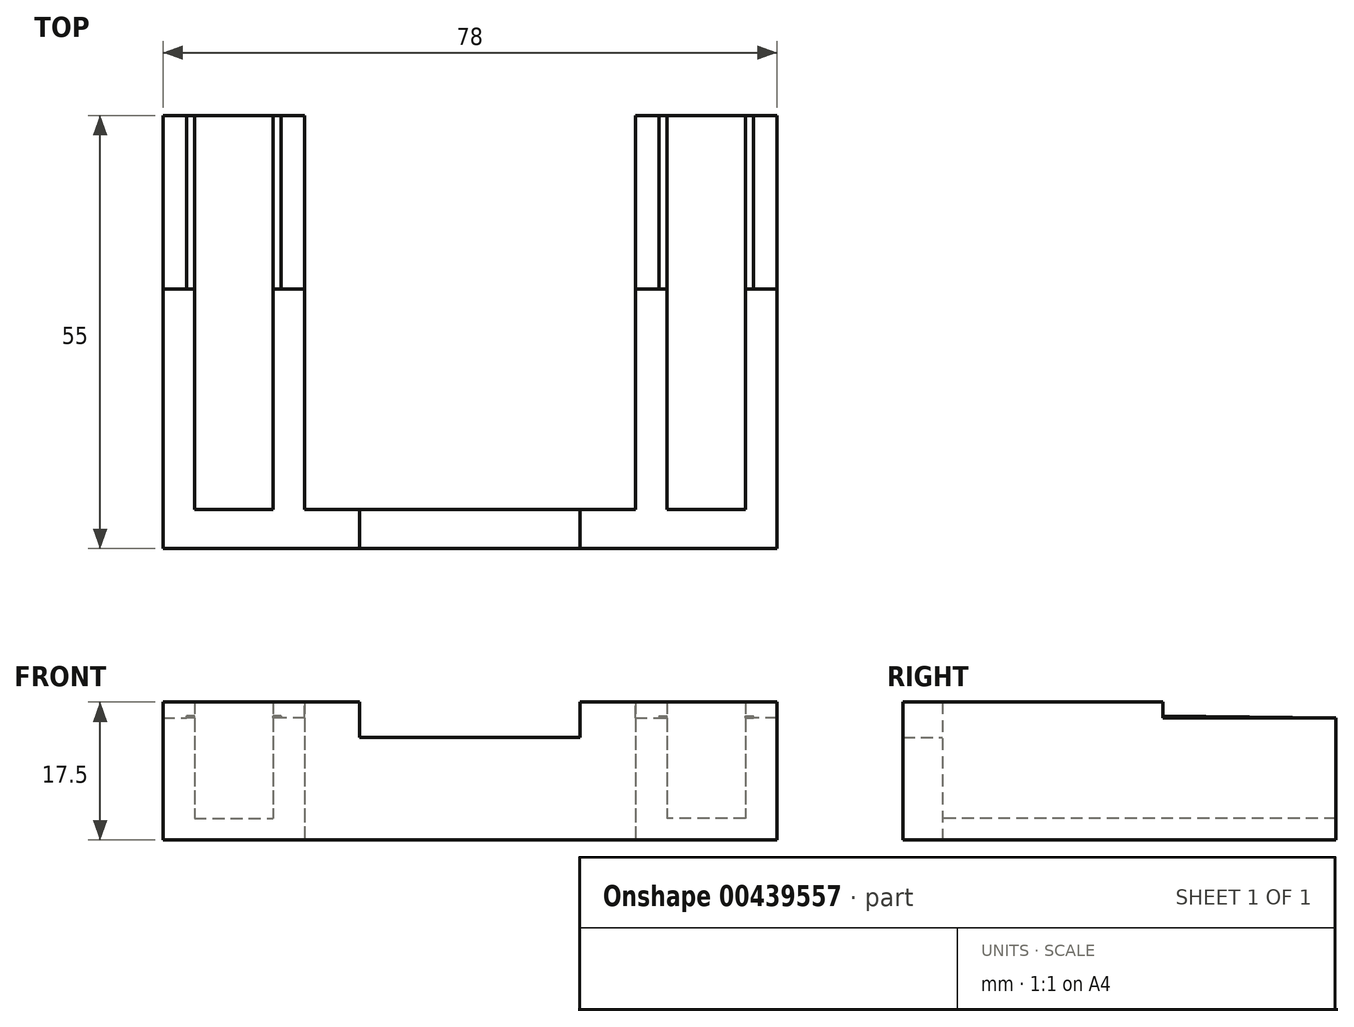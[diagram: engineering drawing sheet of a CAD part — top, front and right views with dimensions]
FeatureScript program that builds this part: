
annotation { "Feature Type Name" : "Feature", "Feature Type Description" : "" }
export const myFeature = defineFeature(function(context is Context, id is Id, definition is map)
    precondition{}
    {
        {
            var Q0;
            Q0=qCreatedBy(makeId("Front.planeOp"),FACE);
            var sketch = newSketch(context, id + "F0", { "sketchPlane" : qUnion([Q0])});
            skLineSegment(sketch, "E0.bottom", {"start": v(-35, 2) * mm, "end": v(-25, 2) * mm});
            skLineSegment(sketch, "E0.top", {"start": v(-35, -2) * mm, "end": v(-25, -2) * mm});
            skLineSegment(sketch, "E1.bottom", {"start": v(-39, 7.75) * mm, "end": v(-35, 7.75) * mm});
            skLineSegment(sketch, "E1.top", {"start": v(-39, -7.75) * mm, "end": v(-35, -7.75) * mm});
            skLineSegment(sketch, "E1.left", {"start": v(-39, 7.75) * mm, "end": v(-39, -7.75) * mm});
            skLineSegment(sketch, "E1.right", {"start": v(-35, 7.75) * mm, "end": v(-35, 2) * mm});
            skLineSegment(sketch, "E2.bottom", {"start": v(-21, 7.75) * mm, "end": v(-25, 7.75) * mm});
            skLineSegment(sketch, "E2.top", {"start": v(-21, -7.75) * mm, "end": v(-25, -7.75) * mm});
            skLineSegment(sketch, "E2.left", {"start": v(-21, 7.75) * mm, "end": v(-21, -7.75) * mm});
            skLineSegment(sketch, "E2.right", {"start": v(-25, 7.75) * mm, "end": v(-25, 2) * mm});
            skLineSegment(sketch, "E3.trimOffspring", {"start": v(-25, -2) * mm, "end": v(-25, -7.75) * mm});
            skLineSegment(sketch, "E4.trimOffspring", {"start": v(-35, -2) * mm, "end": v(-35, -7.75) * mm});
            skPoint(sketch, "E5.trimOffspring.start.orphan", {"position": v(-21, -2) * mm});
            skPoint(sketch, "E6.orphan", {"position": v(-39, 2) * mm});
            skPoint(sketch, "E7.orphan", {"position": v(-21, 2) * mm});
            skPoint(sketch, "E8.visualSharp", {"position": v(-39, 7.75) * mm});
            skPoint(sketch, "E9.visualSharp", {"position": v(-35, 7.75) * mm});
            skPoint(sketch, "E10.visualSharp", {"position": v(-35, 2) * mm});
            skPoint(sketch, "E11.visualSharp", {"position": v(-25, 2) * mm});
            skPoint(sketch, "E12.visualSharp", {"position": v(-25, 7.75) * mm});
            skPoint(sketch, "E13.visualSharp", {"position": v(-21, 7.75) * mm});
            skPoint(sketch, "E14.visualSharp", {"position": v(-21, -7.75) * mm});
            skPoint(sketch, "E15.visualSharp", {"position": v(-25, -7.75) * mm});
            skPoint(sketch, "E16.visualSharp", {"position": v(-25, -2) * mm});
            skPoint(sketch, "E17.visualSharp", {"position": v(-35, -2) * mm});
            skPoint(sketch, "E18.visualSharp", {"position": v(-35, -7.75) * mm});
            skPoint(sketch, "E19.visualSharp", {"position": v(-39, -7.75) * mm});
            skSolve(sketch);
        }
        {
            var Q0;
            Q0=makeQuery(id+"F0.imprint","IMPRINT",FACE,{"disambiguationData":[TD([[makeQuery(id+"F0.imprint","IMPRINT",EDGE,{"derivedFrom":sQuery(id+"F0.wireOp",EDGE,"E0.bottom")}),-1.0]])]});
            extrude(context, id + "F1", {"entities" : qUnion([Q0]), "oppositeDirection" : true, "depth" : 40 * mm});
        }
        {
            var Q0;
            Q0=makeQuery(id+"F1.opExtrude","CAP_FACE",FACE,{"disambiguationData":[OSD([sQuery(id+"F0.wireOp",EDGE,"E0.bottom"),sQuery(id+"F0.wireOp",EDGE,"E0.top"),sQuery(id+"F0.wireOp",EDGE,"E1.bottom"),sQuery(id+"F0.wireOp",EDGE,"E1.top"),sQuery(id+"F0.wireOp",EDGE,"E1.left"),sQuery(id+"F0.wireOp",EDGE,"E1.right"),sQuery(id+"F0.wireOp",EDGE,"E2.bottom"),sQuery(id+"F0.wireOp",EDGE,"E2.top"),sQuery(id+"F0.wireOp",EDGE,"E2.left"),sQuery(id+"F0.wireOp",EDGE,"E2.right"),sQuery(id+"F0.wireOp",EDGE,"E3.trimOffspring"),sQuery(id+"F0.wireOp",EDGE,"E4.trimOffspring"),sQuery(id+"F0.wireOp",EDGE,"E8.filletArc"),sQuery(id+"F0.wireOp",EDGE,"E9.filletArc"),sQuery(id+"F0.wireOp",EDGE,"E10.filletArc"),sQuery(id+"F0.wireOp",EDGE,"E11.filletArc"),sQuery(id+"F0.wireOp",EDGE,"E12.filletArc"),sQuery(id+"F0.wireOp",EDGE,"E13.filletArc"),sQuery(id+"F0.wireOp",EDGE,"E14.filletArc"),sQuery(id+"F0.wireOp",EDGE,"E15.filletArc"),sQuery(id+"F0.wireOp",EDGE,"E16.filletArc"),sQuery(id+"F0.wireOp",EDGE,"E17.filletArc"),sQuery(id+"F0.wireOp",EDGE,"E18.filletArc"),sQuery(id+"F0.wireOp",EDGE,"E19.filletArc")])],"isStart":true});
            var sketch = newSketch(context, id + "F2", { "sketchPlane" : qUnion([Q0])});
            skLineSegment(sketch, "E20.bottom", {"start": v(-39, 7.75) * mm, "end": v(-35, 7.75) * mm});
            skLineSegment(sketch, "E20.top", {"start": v(-39, 8.25) * mm, "end": v(-35, 8.25) * mm});
            skLineSegment(sketch, "E20.left", {"start": v(-39, 7.75) * mm, "end": v(-39, 8.25) * mm});
            skLineSegment(sketch, "E20.right", {"start": v(-35, 7.75) * mm, "end": v(-35, 8.25) * mm});
            skLineSegment(sketch, "E21.bottom", {"start": v(-25, 7.75) * mm, "end": v(-21, 7.75) * mm});
            skLineSegment(sketch, "E21.top", {"start": v(-25, 8.25) * mm, "end": v(-21, 8.25) * mm});
            skLineSegment(sketch, "E21.left", {"start": v(-25, 7.75) * mm, "end": v(-25, 8.25) * mm});
            skLineSegment(sketch, "E21.right", {"start": v(-21, 7.75) * mm, "end": v(-21, 8.25) * mm});
            skSolve(sketch);
        }
        {
            var Q0;
            Q0=makeQuery(id+"F2.imprint","IMPRINT",FACE,{"disambiguationData":[TD([[makeQuery(id+"F2.imprint","IMPRINT",EDGE,{"derivedFrom":sQuery(id+"F2.wireOp",EDGE,"E20.bottom")}),1.0]])]});
            var Q1;
            Q1=makeQuery(id+"F2.imprint","IMPRINT",FACE,{"disambiguationData":[TD([[makeQuery(id+"F2.imprint","IMPRINT",EDGE,{"derivedFrom":sQuery(id+"F2.wireOp",EDGE,"E21.bottom")}),-1.0]])]});
            extrude(context, id + "F3", {"entities" : qUnion([Q0, Q1]), "operationType" : NewBodyOperationType.ADD, "oppositeDirection" : true, "depth" : 18 * mm});
        }
        {
            var Q0;
            {var subQ0=sQuery(id+"F0.wireOp",EDGE,"E19.filletArc");var subQ1=sQuery(id+"F0.wireOp",EDGE,"E18.filletArc");var subQ2=sQuery(id+"F0.wireOp",EDGE,"E17.filletArc");var subQ3=sQuery(id+"F0.wireOp",EDGE,"E16.filletArc");var subQ4=sQuery(id+"F0.wireOp",EDGE,"E15.filletArc");var subQ5=sQuery(id+"F0.wireOp",EDGE,"E14.filletArc");var subQ6=sQuery(id+"F0.wireOp",EDGE,"E13.filletArc");var subQ7=sQuery(id+"F0.wireOp",EDGE,"E12.filletArc");var subQ8=sQuery(id+"F0.wireOp",EDGE,"E11.filletArc");var subQ9=sQuery(id+"F0.wireOp",EDGE,"E10.filletArc");var subQ10=sQuery(id+"F0.wireOp",EDGE,"E9.filletArc");var subQ11=sQuery(id+"F0.wireOp",EDGE,"E8.filletArc");var subQ12=sQuery(id+"F0.wireOp",EDGE,"E4.trimOffspring");var subQ13=sQuery(id+"F0.wireOp",EDGE,"E3.trimOffspring");var subQ14=sQuery(id+"F0.wireOp",EDGE,"E2.right");var subQ15=sQuery(id+"F0.wireOp",EDGE,"E2.left");var subQ16=sQuery(id+"F0.wireOp",EDGE,"E2.top");var subQ17=sQuery(id+"F0.wireOp",EDGE,"E2.bottom");var subQ18=sQuery(id+"F0.wireOp",EDGE,"E1.right");var subQ19=sQuery(id+"F0.wireOp",EDGE,"E1.left");var subQ20=sQuery(id+"F0.wireOp",EDGE,"E1.top");var subQ21=sQuery(id+"F0.wireOp",EDGE,"E1.bottom");var subQ22=sQuery(id+"F0.wireOp",EDGE,"E0.top");var subQ23=sQuery(id+"F0.wireOp",EDGE,"E0.bottom");Q0=makeQuery(id+"F3.boolean.opBoolean","MERGE",FACE,{"derivedFrom":[makeQuery(id+"F1.opExtrude","CAP_FACE",FACE,{"disambiguationData":[OSD([subQ23,subQ22,subQ21,subQ20,subQ19,subQ18,subQ17,subQ16,subQ15,subQ14,subQ13,subQ12,subQ11,subQ10,subQ9,subQ8,subQ7,subQ6,subQ5,subQ4,subQ3,subQ2,subQ1,subQ0])],"isStart":true}),makeQuery(id+"F3.opExtrude","CAP_FACE",FACE,{"disambiguationData":[OSD([subQ23,subQ22,subQ21,subQ20,subQ19,subQ18,subQ17,subQ16,subQ15,subQ14,subQ13,subQ12,subQ11,subQ10,subQ9,subQ8,subQ7,subQ6,subQ5,subQ4,subQ3,subQ2,subQ1,subQ0,sQuery(id+"F2.wireOp",EDGE,"e74bea4d-e17d-4530-9acc-5db0af419567.0"),sQuery(id+"F2.wireOp",EDGE,"e74bea4d-e17d-4530-9acc-5db0af419567.1"),sQuery(id+"F2.wireOp",EDGE,"e74bea4d-e17d-4530-9acc-5db0af419567.2"),sQuery(id+"F2.wireOp",EDGE,"e74bea4d-e17d-4530-9acc-5db0af419567.3"),sQuery(id+"F2.wireOp",EDGE,"e74bea4d-e17d-4530-9acc-5db0af419567.4"),sQuery(id+"F2.wireOp",EDGE,"e74bea4d-e17d-4530-9acc-5db0af419567.5"),sQuery(id+"F2.wireOp",EDGE,"e74bea4d-e17d-4530-9acc-5db0af419567.6"),sQuery(id+"F2.wireOp",EDGE,"e74bea4d-e17d-4530-9acc-5db0af419567.7"),sQuery(id+"F2.wireOp",EDGE,"e74bea4d-e17d-4530-9acc-5db0af419567.8"),sQuery(id+"F2.wireOp",EDGE,"e74bea4d-e17d-4530-9acc-5db0af419567.9"),sQuery(id+"F2.wireOp",EDGE,"e74bea4d-e17d-4530-9acc-5db0af419567.10"),sQuery(id+"F2.wireOp",EDGE,"e74bea4d-e17d-4530-9acc-5db0af419567.11"),sQuery(id+"F2.wireOp",EDGE,"e74bea4d-e17d-4530-9acc-5db0af419567.12"),sQuery(id+"F2.wireOp",EDGE,"e74bea4d-e17d-4530-9acc-5db0af419567.13"),sQuery(id+"F2.wireOp",EDGE,"e74bea4d-e17d-4530-9acc-5db0af419567.14"),sQuery(id+"F2.wireOp",EDGE,"e74bea4d-e17d-4530-9acc-5db0af419567.15"),sQuery(id+"F2.wireOp",EDGE,"e74bea4d-e17d-4530-9acc-5db0af419567.16"),sQuery(id+"F2.wireOp",EDGE,"e74bea4d-e17d-4530-9acc-5db0af419567.17"),sQuery(id+"F2.wireOp",EDGE,"e74bea4d-e17d-4530-9acc-5db0af419567.18"),sQuery(id+"F2.wireOp",EDGE,"e74bea4d-e17d-4530-9acc-5db0af419567.19"),sQuery(id+"F2.wireOp",EDGE,"e74bea4d-e17d-4530-9acc-5db0af419567.20"),sQuery(id+"F2.wireOp",EDGE,"e74bea4d-e17d-4530-9acc-5db0af419567.21"),sQuery(id+"F2.wireOp",EDGE,"e74bea4d-e17d-4530-9acc-5db0af419567.22"),sQuery(id+"F2.wireOp",EDGE,"e74bea4d-e17d-4530-9acc-5db0af419567.23")])],"isStart":true})]});}
            var sketch = newSketch(context, id + "F4", { "sketchPlane" : qUnion([Q0])});
            skLineSegment(sketch, "E22.bottom", {"start": v(-39, 8.25) * mm, "end": v(-14, 8.25) * mm});
            skLineSegment(sketch, "E22.top", {"start": v(-39, -7.75) * mm, "end": v(-13.5, -7.75) * mm});
            skLineSegment(sketch, "E22.left", {"start": v(-39, 8.25) * mm, "end": v(-39, -7.75) * mm});
            skLineSegment(sketch, "E22.right", {"start": v(0, 5.25) * mm, "end": v(0, -7.75) * mm});
            skPoint(sketch, "E23.visualSharp", {"position": v(-39, 8.25) * mm});
            skPoint(sketch, "E24.visualSharp", {"position": v(-39, -7.75) * mm});
            skLineSegment(sketch, "E25.bottom", {"start": v(-14, 8.25) * mm, "end": v(0, 8.25) * mm});
            skLineSegment(sketch, "E25.top", {"start": v(-14, 5.25) * mm, "end": v(0, 5.25) * mm});
            skLineSegment(sketch, "E25.left", {"start": v(-14, 8.25) * mm, "end": v(-14, 5.25) * mm});
            skLineSegment(sketch, "E25.right", {"start": v(0, 8.25) * mm, "end": v(0, 5.25) * mm});
            skPoint(sketch, "E26.oppositeSnap0", {"position": v(-14, 5.92) * mm});
            skLineSegment(sketch, "E26.top", {"start": v(0, -7.75) * mm, "end": v(-13.5, -7.75) * mm});
            skPoint(sketch, "E27.newPointB", {"position": v(-14, 6.59) * mm});
            skPoint(sketch, "E28.visualSharp", {"position": v(-14, 5.25) * mm});
            skPoint(sketch, "E29.visualSharp", {"position": v(-14, -7.75) * mm});
            skPoint(sketch, "E30.newPointA", {"position": v(0, -7.75) * mm});
            skSolve(sketch);
        }
        {
            var Q0;
            Q0=makeQuery(id+"F1.opExtrude","SWEPT_FACE",FACE,{"disambiguationData":[OSD([sQuery(id+"F0.wireOp",EDGE,"E1.bottom")])]});
            var sketch = newSketch(context, id + "F5", { "sketchPlane" : qUnion([Q0])});
            skLineSegment(sketch, "E31.bottom", {"start": v(-36, 40) * mm, "end": v(-35, 40) * mm});
            skLineSegment(sketch, "E31.top", {"start": v(-36, 18) * mm, "end": v(-35, 18) * mm});
            skLineSegment(sketch, "E31.left", {"start": v(-36, 40) * mm, "end": v(-36, 18) * mm});
            skLineSegment(sketch, "E31.right", {"start": v(-35, 40) * mm, "end": v(-35, 18) * mm});
            skLineSegment(sketch, "E32.bottom", {"start": v(-25, 40) * mm, "end": v(-24, 40) * mm});
            skLineSegment(sketch, "E32.top", {"start": v(-25, 18) * mm, "end": v(-24, 18) * mm});
            skLineSegment(sketch, "E32.left", {"start": v(-25, 40) * mm, "end": v(-25, 18) * mm});
            skLineSegment(sketch, "E32.right", {"start": v(-24, 40) * mm, "end": v(-24, 18) * mm});
            skSolve(sketch);
        }
        {
            var Q0;
            Q0=makeQuery(id+"F5.imprint","IMPRINT",FACE,{"disambiguationData":[TD([[makeQuery(id+"F5.imprint","IMPRINT",EDGE,{"derivedFrom":sQuery(id+"F5.wireOp",EDGE,"E31.bottom")}),-1.0]])]});
            var Q1;
            Q1=makeQuery(id+"F5.imprint","IMPRINT",FACE,{"disambiguationData":[TD([[makeQuery(id+"F5.imprint","IMPRINT",EDGE,{"derivedFrom":sQuery(id+"F5.wireOp",EDGE,"E32.bottom")}),-1.0]])]});
            extrude(context, id + "F6", {"entities" : qUnion([Q0, Q1]), "operationType" : NewBodyOperationType.ADD, "depth" : 0.5 * mm});
        }
        {
            var Q0;
            Q0=makeQuery(id+"F4.imprint","IMPRINT",FACE,{"disambiguationData":[TD([[makeQuery(id+"F4.imprint","IMPRINT",EDGE,{"derivedFrom":makeQuery(id+"F1.opExtrude","CAP_EDGE",EDGE,{"disambiguationData":[OSD([sQuery(id+"F0.wireOp",EDGE,"E0.bottom")])],"isStart":true})}),1.0]])]});
            var Q1;
            {var subQ2=sQuery(id+"F4.wireOp",EDGE,"E22.left");Q1=makeQuery(id+"F4.imprint","IMPRINT",FACE,{"disambiguationData":[TD([[makeQuery(id+"F4.imprint","IMPRINT",EDGE,{"derivedFrom":subQ2}),1.0]])]});}
            var Q2;
            Q2=makeQuery(id+"F4.imprint","IMPRINT",FACE,{"disambiguationData":[TD([[makeQuery(id+"F4.imprint","IMPRINT",EDGE,{"derivedFrom":makeQuery(id+"F1.opExtrude","CAP_EDGE",EDGE,{"disambiguationData":[OSD([sQuery(id+"F0.wireOp",EDGE,"E0.top")])],"isStart":true})}),-1.0]])]});
            var Q3;
            Q3=makeQuery(id+"F4.imprint","IMPRINT",FACE,{"disambiguationData":[TD([[makeQuery(id+"F4.imprint","IMPRINT",EDGE,{"derivedFrom":sQuery(id+"F4.wireOp",EDGE,"E22.right")}),-1.0]])]});
            extrude(context, id + "F7", {"entities" : qUnion([Q0, Q1, Q2, Q3]), "operationType" : NewBodyOperationType.ADD, "depth" : 15 * mm});
        }
        {
            var Q0;
            Q0=makeQuery(id+"F6.opExtrude","SWEPT_FACE",FACE,{"disambiguationData":[OSD([sQuery(id+"F5.wireOp",EDGE,"E31.left")])]});
            var sketch = newSketch(context, id + "F8", { "sketchPlane" : qUnion([Q0])});
            skLineSegment(sketch, "E33", {"start": v(-40, 7.75) * mm, "end": v(-18, 8) * mm});
            skLineSegment(sketch, "E34", {"start": v(-18, 8) * mm, "end": v(-18, 8.25) * mm});
            skLineSegment(sketch, "E35", {"start": v(-18, 8.25) * mm, "end": v(-40, 8.25) * mm});
            skLineSegment(sketch, "E36", {"start": v(-40, 8.25) * mm, "end": v(-40, 7.75) * mm});
            skSolve(sketch);
        }
        {
            var Q0;
            Q0=makeQuery(id+"F8.imprint","IMPRINT",FACE,{"disambiguationData":[TD([[makeQuery(id+"F8.imprint","IMPRINT",EDGE,{"derivedFrom":sQuery(id+"F8.wireOp",EDGE,"E33")}),1.0]])]});
            extrude(context, id + "F9", {"entities" : qUnion([Q0]), "operationType" : NewBodyOperationType.REMOVE, "endBound" : BoundingType.THROUGH_ALL, "oppositeDirection" : true, "depth" : 25 * mm});
        }
        {
            var Q0;
            Q0=makeQuery(id+"F1.opExtrude","SWEPT_FACE",FACE,{"disambiguationData":[OSD([sQuery(id+"F0.wireOp",EDGE,"E0.top")])]});
            var Q1;
            Q1=makeQuery(id+"F7.boolean.opBoolean","MERGE",FACE,{"derivedFrom":[makeQuery(id+"F1.opExtrude","SWEPT_FACE",FACE,{"disambiguationData":[OSD([sQuery(id+"F0.wireOp",EDGE,"E1.top")])]}),makeQuery(id+"F1.opExtrude","SWEPT_FACE",FACE,{"disambiguationData":[OSD([sQuery(id+"F0.wireOp",EDGE,"E2.top")])]}),makeQuery(id+"F7.opExtrude","SWEPT_FACE",FACE,{"disambiguationData":[OSD([sQuery(id+"F4.wireOp",EDGE,"E22.top"),sQuery(id+"F4.wireOp",EDGE,"E26.top")])]})]});
            extrude(context, id + "F10", {"entities" : qUnion([Q0]), "operationType" : NewBodyOperationType.ADD, "endBound" : BoundingType.UP_TO_SURFACE, "endBoundEntityFace" : qUnion([Q1]), "depth" : 25 * mm});
        }
        {
            var Q0;
            Q0=makeQuery(id+"F1.opExtrude","SWEPT_FACE",FACE,{"disambiguationData":[OSD([sQuery(id+"F0.wireOp",EDGE,"E0.bottom")])]});
            extrude(context, id + "F11", {"entities" : qUnion([Q0]), "operationType" : NewBodyOperationType.REMOVE, "oppositeDirection" : true, "depth" : 7 * mm});
        }
        {
            var Q0;
            {var subQ0=sQuery(id+"F0.wireOp",EDGE,"E0.bottom");var subQ2=sQuery(id+"F4.wireOp",EDGE,"E22.bottom");Q0=makeQuery(id+"F11.boolean.opBoolean","MERGE",FACE,{"derivedFrom":[makeQuery(id+"F7.boolean.opBoolean","SPLIT",FACE,{"disambiguationData":[TD([makeQuery(id+"F1.opExtrude","SWEPT_FACE",FACE,{"disambiguationData":[OSD([subQ0])]})])],"derivedFrom":makeQuery(id+"F7.opExtrude","CAP_FACE",FACE,{"disambiguationData":[OSD([subQ2,sQuery(id+"F4.wireOp",EDGE,"E22.top"),sQuery(id+"F4.wireOp",EDGE,"E22.left"),sQuery(id+"F4.wireOp",EDGE,"E22.right"),sQuery(id+"F4.wireOp",EDGE,"E25.top"),sQuery(id+"F4.wireOp",EDGE,"E25.left"),sQuery(id+"F4.wireOp",EDGE,"E26.top"),sQuery(id+"F4.wireOp",EDGE,"E27.filletArc"),sQuery(id+"F4.wireOp",EDGE,"E28.filletArc")])],"isStart":true})}),makeQuery(id+"F11.opExtrude","SWEPT_FACE",FACE,{"disambiguationData":[OSD([subQ0]),TDD([makeQuery(id+"F1.opExtrude","CAP_EDGE",EDGE,{"disambiguationData":[OSD([subQ0])],"isStart":true})])]})]});}
            var Q1;
            {var subQ0=sQuery(id+"F4.wireOp",EDGE,"E26.top");var subQ1=sQuery(id+"F4.wireOp",EDGE,"E22.top");var subQ2=sQuery(id+"F4.wireOp",EDGE,"E22.bottom");var subQ3=sQuery(id+"F4.wireOp",EDGE,"E27.filletArc");var subQ4=sQuery(id+"F4.wireOp",EDGE,"E25.left");var subQ5=sQuery(id+"F4.wireOp",EDGE,"E25.top");var subQ6=sQuery(id+"F4.wireOp",EDGE,"E22.right");var subQ7=sQuery(id+"F4.wireOp",EDGE,"E28.filletArc");Q1=makeQuery(id+"F7.boolean.opBoolean","SPLIT",FACE,{"disambiguationData":[TD([makeQuery(id+"F1.opExtrude","SWEPT_FACE",FACE,{"disambiguationData":[OSD([sQuery(id+"F0.wireOp",EDGE,"E2.left")])]})])],"derivedFrom":makeQuery(id+"F7.opExtrude","CAP_FACE",FACE,{"disambiguationData":[OSD([subQ2,subQ1,sQuery(id+"F4.wireOp",EDGE,"E22.left"),subQ6,subQ5,subQ4,subQ0,subQ3,subQ7])],"isStart":true})});}
            extrude(context, id + "F12", {"entities" : qUnion([Q0, Q1]), "operationType" : NewBodyOperationType.REMOVE, "oppositeDirection" : true, "depth" : 10 * mm});
        }
        {
            var Q0;
            Q0=makeQuery(id+"F1.opExtrude","SWEPT_BODY",BODY,{"disambiguationData":[OSD([sQuery(id+"F0.wireOp",EDGE,"E0.bottom"),sQuery(id+"F0.wireOp",EDGE,"E0.top"),sQuery(id+"F0.wireOp",EDGE,"E1.bottom"),sQuery(id+"F0.wireOp",EDGE,"E1.top"),sQuery(id+"F0.wireOp",EDGE,"E1.left"),sQuery(id+"F0.wireOp",EDGE,"E1.right"),sQuery(id+"F0.wireOp",EDGE,"E2.bottom"),sQuery(id+"F0.wireOp",EDGE,"E2.top"),sQuery(id+"F0.wireOp",EDGE,"E2.left"),sQuery(id+"F0.wireOp",EDGE,"E2.right"),sQuery(id+"F0.wireOp",EDGE,"E3.trimOffspring"),sQuery(id+"F0.wireOp",EDGE,"E4.trimOffspring"),sQuery(id+"F0.wireOp",EDGE,"E8.filletArc"),sQuery(id+"F0.wireOp",EDGE,"E9.filletArc"),sQuery(id+"F0.wireOp",EDGE,"E10.filletArc"),sQuery(id+"F0.wireOp",EDGE,"E11.filletArc"),sQuery(id+"F0.wireOp",EDGE,"E12.filletArc"),sQuery(id+"F0.wireOp",EDGE,"E13.filletArc"),sQuery(id+"F0.wireOp",EDGE,"E14.filletArc"),sQuery(id+"F0.wireOp",EDGE,"E15.filletArc"),sQuery(id+"F0.wireOp",EDGE,"E16.filletArc"),sQuery(id+"F0.wireOp",EDGE,"E17.filletArc"),sQuery(id+"F0.wireOp",EDGE,"E18.filletArc"),sQuery(id+"F0.wireOp",EDGE,"E19.filletArc")])]});
            var Q1;
            Q1=qCreatedBy(makeId("Right.planeOp"),FACE);
            mirror(context, id + "F13", {"operationType" : NewBodyOperationType.ADD, "entities" : qUnion([Q0]), "mirrorPlane" : qUnion([Q1])});
        }
        {
            var Q0;
            Q0=makeQuery(id+"F7.boolean.opBoolean","MERGE",FACE,{"derivedFrom":[makeQuery(id+"F6.boolean.opBoolean","MERGE",FACE,{"derivedFrom":[makeQuery(id+"F3.opExtrude","SWEPT_FACE",FACE,{"disambiguationData":[OSD([sQuery(id+"F2.wireOp",EDGE,"E20.top")])]}),makeQuery(id+"F6.opExtrude","CAP_FACE",FACE,{"disambiguationData":[OSD([sQuery(id+"F5.wireOp",EDGE,"E31.bottom"),sQuery(id+"F5.wireOp",EDGE,"E31.top"),sQuery(id+"F5.wireOp",EDGE,"E31.left"),sQuery(id+"F5.wireOp",EDGE,"E31.right")])],"isStart":false})]}),makeQuery(id+"F6.boolean.opBoolean","MERGE",FACE,{"derivedFrom":[makeQuery(id+"F3.opExtrude","SWEPT_FACE",FACE,{"disambiguationData":[OSD([sQuery(id+"F2.wireOp",EDGE,"E21.top")])]}),makeQuery(id+"F6.opExtrude","CAP_FACE",FACE,{"disambiguationData":[OSD([sQuery(id+"F5.wireOp",EDGE,"E32.bottom"),sQuery(id+"F5.wireOp",EDGE,"E32.top"),sQuery(id+"F5.wireOp",EDGE,"E32.left"),sQuery(id+"F5.wireOp",EDGE,"E32.right")])],"isStart":false})]}),makeQuery(id+"F7.opExtrude","SWEPT_FACE",FACE,{"disambiguationData":[OSD([sQuery(id+"F4.wireOp",EDGE,"E22.bottom")])]})]});
            var Q1;
            Q1=makeQuery(id+"F13.opPattern","COPY",FACE,{"derivedFrom":makeQuery(id+"F7.boolean.opBoolean","MERGE",FACE,{"derivedFrom":[makeQuery(id+"F6.boolean.opBoolean","MERGE",FACE,{"derivedFrom":[makeQuery(id+"F3.opExtrude","SWEPT_FACE",FACE,{"disambiguationData":[OSD([sQuery(id+"F2.wireOp",EDGE,"E20.top")])]}),makeQuery(id+"F6.opExtrude","CAP_FACE",FACE,{"disambiguationData":[OSD([sQuery(id+"F5.wireOp",EDGE,"E31.bottom"),sQuery(id+"F5.wireOp",EDGE,"E31.top"),sQuery(id+"F5.wireOp",EDGE,"E31.left"),sQuery(id+"F5.wireOp",EDGE,"E31.right")])],"isStart":false})]}),makeQuery(id+"F6.boolean.opBoolean","MERGE",FACE,{"derivedFrom":[makeQuery(id+"F3.opExtrude","SWEPT_FACE",FACE,{"disambiguationData":[OSD([sQuery(id+"F2.wireOp",EDGE,"E21.top")])]}),makeQuery(id+"F6.opExtrude","CAP_FACE",FACE,{"disambiguationData":[OSD([sQuery(id+"F5.wireOp",EDGE,"E32.bottom"),sQuery(id+"F5.wireOp",EDGE,"E32.top"),sQuery(id+"F5.wireOp",EDGE,"E32.left"),sQuery(id+"F5.wireOp",EDGE,"E32.right")])],"isStart":false})]}),makeQuery(id+"F7.opExtrude","SWEPT_FACE",FACE,{"disambiguationData":[OSD([sQuery(id+"F4.wireOp",EDGE,"E22.bottom")])]})]}),"instanceName":"1"});
            extrude(context, id + "F14", {"entities" : qUnion([Q0, Q1]), "operationType" : NewBodyOperationType.ADD, "depth" : 1.5 * mm});
        }
    });
